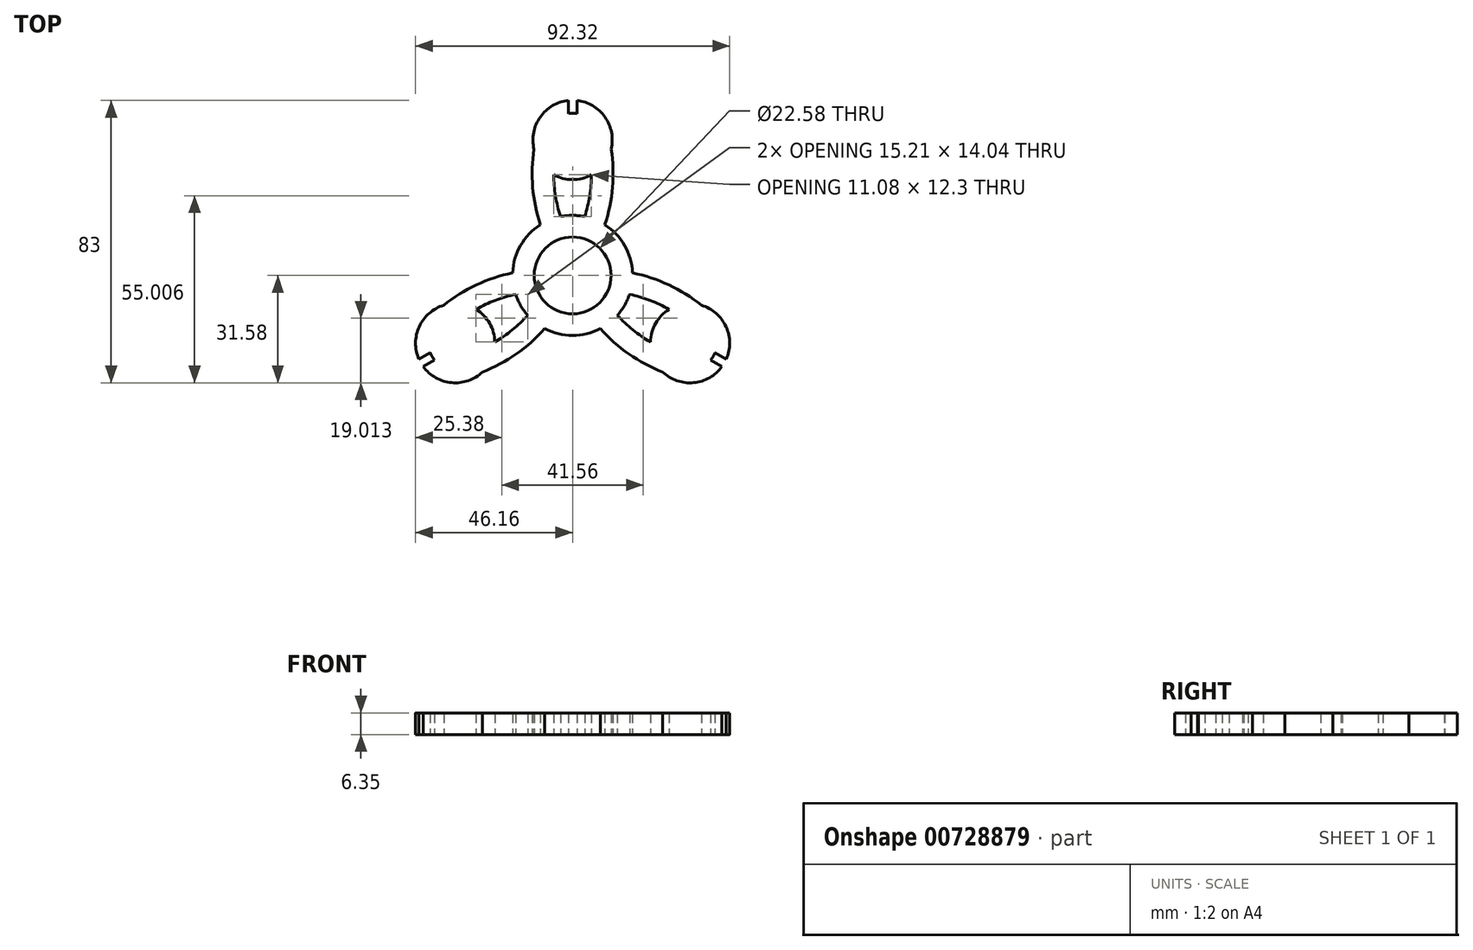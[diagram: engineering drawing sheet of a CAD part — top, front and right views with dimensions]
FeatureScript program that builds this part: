
annotation { "Feature Type Name" : "Feature", "Feature Type Description" : "" }
export const myFeature = defineFeature(function(context is Context, id is Id, definition is map)
    precondition{}
    {
        {
            var Q0;
            Q0=qCreatedBy(makeId("Top.planeOp"),FACE);
            var sketch = newSketch(context, id + "F0", { "sketchPlane" : qUnion([Q0])});
            skCircle(sketch, "E0", {"center": v(0, 0) * mm, "radius": 11.3 * mm});
            skArc(sketch, "E1.0", {"start": v(-9.47, 14.88) * mm, "mid": v(-15.46, 8.49) * mm, "end": v(-17.64, 0) * mm});
            skArc(sketch, "E2", {"start": v(-11.35, 37.15) * mm, "mid": v(-11.72, 25.9) * mm, "end": v(-9.47, 14.88) * mm});
            skArc(sketch, "E3.trimOffspring", {"start": v(-5.54, 29.58) * mm, "mid": v(-5.02, 23.35) * mm, "end": v(-3.57, 17.28) * mm});
            skArc(sketch, "E4.MirrorCS", {"start": v(5.54, 29.58) * mm, "mid": v(5.02, 23.35) * mm, "end": v(3.57, 17.28) * mm});
            skArc(sketch, "E5.MirrorCS", {"start": v(11.35, 37.15) * mm, "mid": v(11.72, 25.9) * mm, "end": v(9.47, 14.88) * mm});
            skArc(sketch, "E6.trimOffspring", {"start": v(3.57, 17.28) * mm, "mid": v(0, 17.64) * mm, "end": v(-3.57, 17.28) * mm});
            skArc(sketch, "E7.1.0", {"start": v(-37.85, -8.75) * mm, "mid": v(-28.3, -2.8) * mm, "end": v(-17.62, 0.76) * mm});
            skArc(sketch, "E7.1.3", {"start": v(-26.5, -28.4) * mm, "mid": v(-16.57, -23.1) * mm, "end": v(-8.15, -15.64) * mm});
            skArc(sketch, "E7.1.4", {"start": v(-22.84, -19.59) * mm, "mid": v(-17.71, -16.02) * mm, "end": v(-13.18, -11.73) * mm});
            skArc(sketch, "E7.1.5", {"start": v(-28.38, -9.99) * mm, "mid": v(-22.73, -7.33) * mm, "end": v(-16.75, -5.55) * mm});
            skArc(sketch, "E7.2.0", {"start": v(26.5, -28.4) * mm, "mid": v(16.57, -23.1) * mm, "end": v(8.15, -15.64) * mm});
            skArc(sketch, "E7.2.3", {"start": v(37.85, -8.75) * mm, "mid": v(28.3, -2.8) * mm, "end": v(17.62, 0.76) * mm});
            skArc(sketch, "E7.2.4", {"start": v(28.38, -9.99) * mm, "mid": v(22.73, -7.33) * mm, "end": v(16.75, -5.55) * mm});
            skArc(sketch, "E7.2.5", {"start": v(22.84, -19.59) * mm, "mid": v(17.71, -16.02) * mm, "end": v(13.18, -11.73) * mm});
            skArc(sketch, "E8.trimOffspring", {"start": v(-16.75, -5.55) * mm, "mid": v(-15.28, -8.82) * mm, "end": v(-13.18, -11.73) * mm});
            skArc(sketch, "E9.trimOffspring", {"start": v(-8.15, -15.64) * mm, "mid": v(0, -17.64) * mm, "end": v(8.15, -15.64) * mm});
            skArc(sketch, "E10.trimOffspring", {"start": v(13.18, -11.73) * mm, "mid": v(15.28, -8.82) * mm, "end": v(16.75, -5.55) * mm});
            skArc(sketch, "E11.trimOffspring", {"start": v(17.64, 0) * mm, "mid": v(15.46, 8.49) * mm, "end": v(9.47, 14.88) * mm});
            skArc(sketch, "E12.0", {"start": v(-1.27, 51.42) * mm, "mid": v(-9.52, 46.56) * mm, "end": v(-11.35, 37.15) * mm});
            skArc(sketch, "E13.1.0", {"start": v(-37.85, -8.75) * mm, "mid": v(-45.08, -15.03) * mm, "end": v(-45.17, -24.61) * mm});
            skArc(sketch, "E13.2.0", {"start": v(28.38, -9.99) * mm, "mid": v(24.4, -14.09) * mm, "end": v(22.84, -19.59) * mm});
            skPoint(sketch, "E14.orphan", {"position": v(40.17, -10.74) * mm});
            skPoint(sketch, "E15.orphan", {"position": v(29.24, -10.49) * mm});
            skPoint(sketch, "E16.orphan", {"position": v(29.38, -29.42) * mm});
            skArc(sketch, "E17.trimOffspring", {"start": v(26.5, -28.4) * mm, "mid": v(35.56, -31.53) * mm, "end": v(43.9, -26.81) * mm});
            skPoint(sketch, "E18.orphan", {"position": v(23.7, -20.08) * mm});
            skPoint(sketch, "E19.orphan", {"position": v(-40.17, -10.74) * mm});
            skPoint(sketch, "E20.orphan", {"position": v(-29.24, -10.49) * mm});
            skPoint(sketch, "E21.orphan", {"position": v(-23.7, -20.08) * mm});
            skArc(sketch, "E22.trimOffspring", {"start": v(-22.84, -19.59) * mm, "mid": v(-24.4, -14.09) * mm, "end": v(-28.38, -9.99) * mm});
            skPoint(sketch, "E23.orphan", {"position": v(-29.38, -29.42) * mm});
            skPoint(sketch, "E24.orphan", {"position": v(-10.8, 40.16) * mm});
            skPoint(sketch, "E25.orphan", {"position": v(5.54, 30.57) * mm});
            skPoint(sketch, "E26.orphan", {"position": v(-5.54, 30.57) * mm});
            skPoint(sketch, "E27.orphan", {"position": v(10.8, 40.16) * mm});
            skLineSegment(sketch, "E28.0", {"start": v(-1.27, 51.42) * mm, "end": v(-1.27, 47.58) * mm});
            skLineSegment(sketch, "E29.0", {"start": v(1.27, 51.42) * mm, "end": v(1.27, 47.58) * mm});
            skPoint(sketch, "E30.start.orphan", {"position": v(0, 56) * mm});
            skLineSegment(sketch, "E31.1.0", {"start": v(-45.17, -24.61) * mm, "end": v(-41.84, -22.69) * mm});
            skLineSegment(sketch, "E31.1.1", {"start": v(-43.9, -26.81) * mm, "end": v(-40.57, -24.89) * mm});
            skLineSegment(sketch, "E31.2.0", {"start": v(43.9, -26.81) * mm, "end": v(40.57, -24.89) * mm});
            skLineSegment(sketch, "E31.2.1", {"start": v(45.17, -24.61) * mm, "end": v(41.84, -22.69) * mm});
            skArc(sketch, "E32.trimOffspring", {"start": v(-43.9, -26.81) * mm, "mid": v(-35.56, -31.53) * mm, "end": v(-26.5, -28.4) * mm});
            skArc(sketch, "E33.trimOffspring", {"start": v(45.17, -24.61) * mm, "mid": v(45.08, -15.03) * mm, "end": v(37.85, -8.75) * mm});
            skArc(sketch, "E34.trimOffspring", {"start": v(-5.54, 29.58) * mm, "mid": v(0, 28.17) * mm, "end": v(5.54, 29.58) * mm});
            skArc(sketch, "E35.trimOffspring", {"start": v(11.35, 37.15) * mm, "mid": v(0, 51.5) * mm, "end": v(-11.35, 37.15) * mm});
            skCircle(sketch, "E36.converted", {"center": v(0, 39.83) * mm, "radius": 7.85 * mm});
            skCircle(sketch, "E37.converted", {"center": v(-34.5, -19.92) * mm, "radius": 7.85 * mm});
            skCircle(sketch, "E38.converted", {"center": v(34.5, -19.92) * mm, "radius": 7.85 * mm});
            skSolve(sketch);
        }
        {
            var Q0;
            Q0=makeQuery(id+"F0.imprint","IMPRINT",FACE,{"disambiguationData":[TD([[makeQuery(id+"F0.imprint","IMPRINT",EDGE,{"derivedFrom":sQuery(id+"F0.wireOp",EDGE,"E0")}),-1.0]])]});
            var Q1;
            {var subQ0=sQuery(id+"F0.wireOp",EDGE,"E37.converted");var subQ1=makeQuery(id+"F0.imprint","INTERSECT",VERTEX,{"derivedFrom":[sQuery(id+"F0.wireOp",EDGE,"E31.1.0"),subQ0]});Q1=makeQuery(id+"F0.imprint","IMPRINT",FACE,{"disambiguationData":[TD([[makeQuery(id+"F0.imprint","IMPRINT",EDGE,{"disambiguationData":[TD([[subQ1,-1.0]])],"derivedFrom":subQ0}),1.0]])]});}
            var Q2;
            {var subQ0=sQuery(id+"F0.wireOp",EDGE,"E36.converted");var subQ1=makeQuery(id+"F0.imprint","INTERSECT",VERTEX,{"derivedFrom":[sQuery(id+"F0.wireOp",EDGE,"E28.0"),subQ0]});Q2=makeQuery(id+"F0.imprint","IMPRINT",FACE,{"disambiguationData":[TD([[makeQuery(id+"F0.imprint","IMPRINT",EDGE,{"disambiguationData":[TD([[subQ1,1.0]])],"derivedFrom":subQ0}),1.0]])]});}
            var Q3;
            {var subQ0=sQuery(id+"F0.wireOp",EDGE,"E38.converted");var subQ1=makeQuery(id+"F0.imprint","INTERSECT",VERTEX,{"derivedFrom":[sQuery(id+"F0.wireOp",EDGE,"E31.2.0"),subQ0]});Q3=makeQuery(id+"F0.imprint","IMPRINT",FACE,{"disambiguationData":[TD([[makeQuery(id+"F0.imprint","IMPRINT",EDGE,{"disambiguationData":[TD([[subQ1,-1.0]])],"derivedFrom":subQ0}),1.0]])]});}
            extrude(context, id + "F1", {"entities" : qUnion([Q0, Q1, Q2, Q3]), "depth" : 6.35 * mm, "offsetDistance" : 25.4 * mm});
        }
    });
